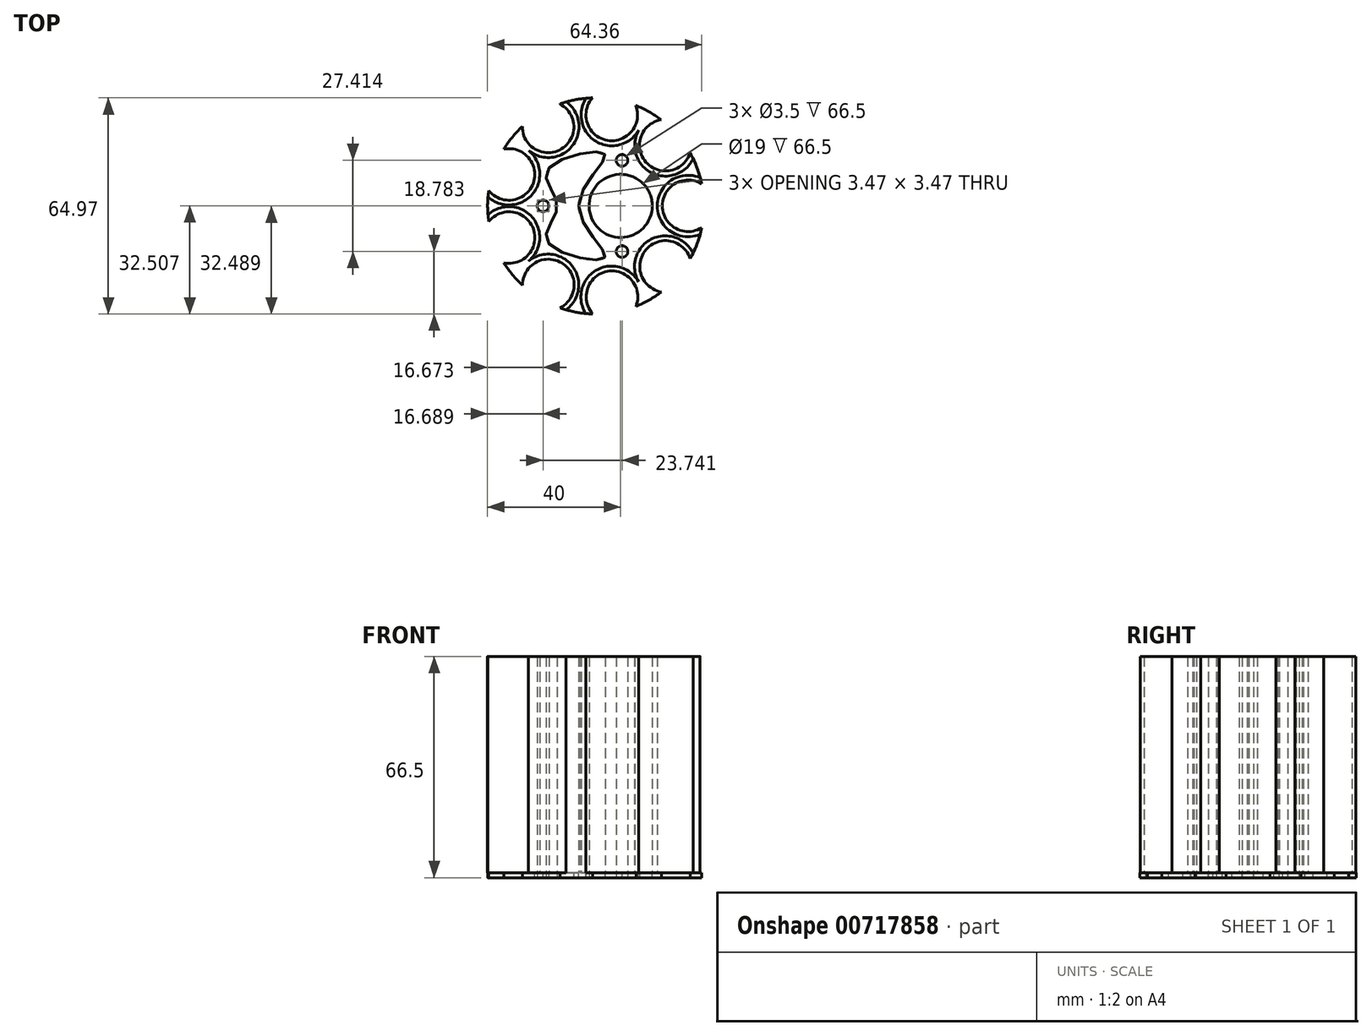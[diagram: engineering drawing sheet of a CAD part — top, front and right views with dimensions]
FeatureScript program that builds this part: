
annotation { "Feature Type Name" : "Feature", "Feature Type Description" : "" }
export const myFeature = defineFeature(function(context is Context, id is Id, definition is map)
    precondition{}
    {
        {
            var Q0;
            Q0=qCreatedBy(makeId("Top.planeOp"),FACE);
            var sketch = newSketch(context, id + "F0", { "sketchPlane" : qUnion([Q0])});
            skCircle(sketch, "E0", {"center": v(0, 0) * mm, "radius": 32.5 * mm});
            skCircle(sketch, "E1", {"center": v(27.75, -0.04) * mm, "radius": 9.25 * mm});
            skCircle(sketch, "E2.1.0", {"center": v(20.95, 18.2) * mm, "radius": 9.25 * mm});
            skCircle(sketch, "E2.2.0", {"center": v(4.85, 27.32) * mm, "radius": 9.25 * mm});
            skCircle(sketch, "E2.3.0", {"center": v(-14.29, 23.8) * mm, "radius": 9.25 * mm});
            skCircle(sketch, "E2.4.0", {"center": v(-26.06, 9.52) * mm, "radius": 9.25 * mm});
            skCircle(sketch, "E2.5.0", {"center": v(-26.09, -9.46) * mm, "radius": 9.25 * mm});
            skCircle(sketch, "E2.6.0", {"center": v(-14.35, -23.75) * mm, "radius": 9.25 * mm});
            skCircle(sketch, "E2.7.0", {"center": v(4.78, -27.33) * mm, "radius": 9.25 * mm});
            skCircle(sketch, "E2.8.0", {"center": v(20.9, -18.25) * mm, "radius": 9.25 * mm});
            skCircle(sketch, "E3", {"center": v(7.5, 0) * mm, "radius": 9.5 * mm});
            skCircle(sketch, "E4", {"center": v(-15.83, 0) * mm, "radius": 1.75 * mm});
            skCircle(sketch, "E5.1.0", {"center": v(7.91, -13.7) * mm, "radius": 1.75 * mm});
            skCircle(sketch, "E5.2.0", {"center": v(7.91, 13.7) * mm, "radius": 1.75 * mm});
            skPoint(sketch, "E6", {"position": v(2.64, 15.6) * mm});
            skPoint(sketch, "E7.MirrorP", {"position": v(2.64, -15.6) * mm});
            skPoint(sketch, "E8", {"position": v(-5.2, 0) * mm});
            skPoint(sketch, "E9", {"position": v(-11.6, 0) * mm});
            skPoint(sketch, "E10", {"position": v(-14.5, 10.8) * mm});
            skPoint(sketch, "E11.MirrorP", {"position": v(-14.5, -10.8) * mm});
            skFitSpline(sketch, "E12", {"points": [v(-5.2, 0) * mm, v(2.64, 15.6) * mm, v(-14.5, 10.8) * mm, v(-11.6, 0) * mm, v(-14.5, -10.8) * mm, v(2.64, -15.6) * mm, v(-5.2, 0) * mm]});
            skCircle(sketch, "E13", {"center": v(0, 0) * mm, "radius": 37 * mm, "construction": true});
            skSolve(sketch);
        }
        {
            var Q0;
            Q0=makeQuery(id+"F0.imprint","IMPRINT",FACE,{"disambiguationData":[TD([[makeQuery(id+"F0.imprint","IMPRINT",EDGE,{"derivedFrom":sQuery(id+"F0.wireOp",EDGE,"E4")}),-1.0]])]});
            extrude(context, id + "F1", {"entities" : qUnion([Q0]), "depth" : 65 * mm, "offsetDistance" : 25 * mm});
        }
        {
            var Q0;
            Q0=makeQuery(id+"F1.opExtrude","CAP_FACE",FACE,{"disambiguationData":[OSD([sQuery(id+"F0.wireOp",EDGE,"E0"),sQuery(id+"F0.wireOp",EDGE,"E1"),sQuery(id+"F0.wireOp",EDGE,"E2.1.0"),sQuery(id+"F0.wireOp",EDGE,"E2.2.0"),sQuery(id+"F0.wireOp",EDGE,"E2.3.0"),sQuery(id+"F0.wireOp",EDGE,"E2.4.0"),sQuery(id+"F0.wireOp",EDGE,"E2.5.0"),sQuery(id+"F0.wireOp",EDGE,"E2.6.0"),sQuery(id+"F0.wireOp",EDGE,"E2.7.0"),sQuery(id+"F0.wireOp",EDGE,"E2.8.0"),sQuery(id+"F0.wireOp",EDGE,"E3"),sQuery(id+"F0.wireOp",EDGE,"E4"),sQuery(id+"F0.wireOp",EDGE,"E5.1.0"),sQuery(id+"F0.wireOp",EDGE,"E5.2.0"),sQuery(id+"F0.wireOp",EDGE,"E12")])],"isStart":true});
            var sketch = newSketch(context, id + "F2", { "sketchPlane" : qUnion([Q0])});
            skCircle(sketch, "E14", {"center": v(0.03, 0) * mm, "radius": 32.5 * mm});
            skCircle(sketch, "E15", {"center": v(27.78, -0.04) * mm, "radius": 7.75 * mm});
            skCircle(sketch, "E16.1.0", {"center": v(20.98, 18.2) * mm, "radius": 7.75 * mm});
            skCircle(sketch, "E16.2.0", {"center": v(4.88, 27.32) * mm, "radius": 7.75 * mm});
            skCircle(sketch, "E16.3.0", {"center": v(-14.26, 23.8) * mm, "radius": 7.75 * mm});
            skCircle(sketch, "E16.4.0", {"center": v(-26.03, 9.52) * mm, "radius": 7.75 * mm});
            skCircle(sketch, "E16.5.0", {"center": v(-26.06, -9.46) * mm, "radius": 7.75 * mm});
            skCircle(sketch, "E16.6.0", {"center": v(-14.32, -23.75) * mm, "radius": 7.75 * mm});
            skCircle(sketch, "E16.7.0", {"center": v(4.81, -27.33) * mm, "radius": 7.75 * mm});
            skCircle(sketch, "E16.8.0", {"center": v(20.93, -18.25) * mm, "radius": 7.75 * mm});
            skCircle(sketch, "E17", {"center": v(7.53, 0) * mm, "radius": 9.5 * mm});
            skCircle(sketch, "E18", {"center": v(-15.8, 0) * mm, "radius": 1.75 * mm});
            skCircle(sketch, "E19.1.0", {"center": v(7.94, -13.7) * mm, "radius": 1.75 * mm});
            skCircle(sketch, "E19.2.0", {"center": v(7.94, 13.7) * mm, "radius": 1.75 * mm});
            skPoint(sketch, "E20", {"position": v(2.67, 15.6) * mm});
            skPoint(sketch, "E21.MirrorP", {"position": v(2.67, -15.6) * mm});
            skPoint(sketch, "E22", {"position": v(-5.16, 0) * mm});
            skPoint(sketch, "E23", {"position": v(-11.57, 0) * mm});
            skPoint(sketch, "E24", {"position": v(-14.47, 10.8) * mm});
            skPoint(sketch, "E25.MirrorP", {"position": v(-14.47, -10.8) * mm});
            skFitSpline(sketch, "E26", {"points": [v(-5.16, 0) * mm, v(2.67, 15.6) * mm, v(-14.47, 10.8) * mm, v(-11.57, 0) * mm, v(-14.47, -10.8) * mm, v(2.67, -15.6) * mm, v(-5.16, 0) * mm]});
            skSolve(sketch);
        }
        {
            var Q0;
            {var subQ24=sQuery(id+"F0.wireOp",EDGE,"E1");Q0=makeQuery(id+"F2.imprint","IMPRINT",FACE,{"disambiguationData":[TD([[makeQuery(id+"F2.imprint","IMPRINT",EDGE,{"derivedFrom":makeQuery(id+"F1.opExtrude","CAP_EDGE",EDGE,{"disambiguationData":[OSD([subQ24])],"isStart":true})}),-1.0]])]});}
            var Q1;
            {var subQ0=sQuery(id+"F2.wireOp",EDGE,"E16.3.0");var subQ1=sQuery(id+"F2.wireOp",EDGE,"E14");var subQ2=makeQuery(id+"F2.imprint","INTERSECT",VERTEX,{"disambiguationData":[OD(0.0)],"derivedFrom":[subQ1,subQ0]});Q1=makeQuery(id+"F2.imprint","IMPRINT",FACE,{"disambiguationData":[TD([[makeQuery(id+"F2.imprint","IMPRINT",EDGE,{"disambiguationData":[TD([[subQ2,1.0]])],"derivedFrom":subQ1}),1.0]])]});}
            var Q2;
            {var subQ17=sQuery(id+"F0.wireOp",EDGE,"E1");Q2=makeQuery(id+"F2.imprint","IMPRINT",FACE,{"disambiguationData":[TD([[makeQuery(id+"F2.imprint","IMPRINT",EDGE,{"derivedFrom":makeQuery(id+"F1.opExtrude","CAP_EDGE",EDGE,{"disambiguationData":[OSD([subQ17])],"isStart":true})}),1.0]])]});}
            var Q3;
            {var subQ1=sQuery(id+"F2.wireOp",EDGE,"E14");var subQ5=sQuery(id+"F2.wireOp",EDGE,"E16.5.0");var subQ6=makeQuery(id+"F2.imprint","INTERSECT",VERTEX,{"disambiguationData":[OD(0.0)],"derivedFrom":[subQ1,subQ5]});Q3=makeQuery(id+"F2.imprint","IMPRINT",FACE,{"disambiguationData":[TD([[makeQuery(id+"F2.imprint","IMPRINT",EDGE,{"disambiguationData":[TD([[subQ6,1.0]])],"derivedFrom":subQ1}),1.0]])]});}
            extrude(context, id + "F3", {"entities" : qUnion([Q0, Q1, Q2, Q3]), "operationType" : NewBodyOperationType.ADD, "depth" : 1.5 * mm, "offsetDistance" : 25 * mm});
        }
    });
